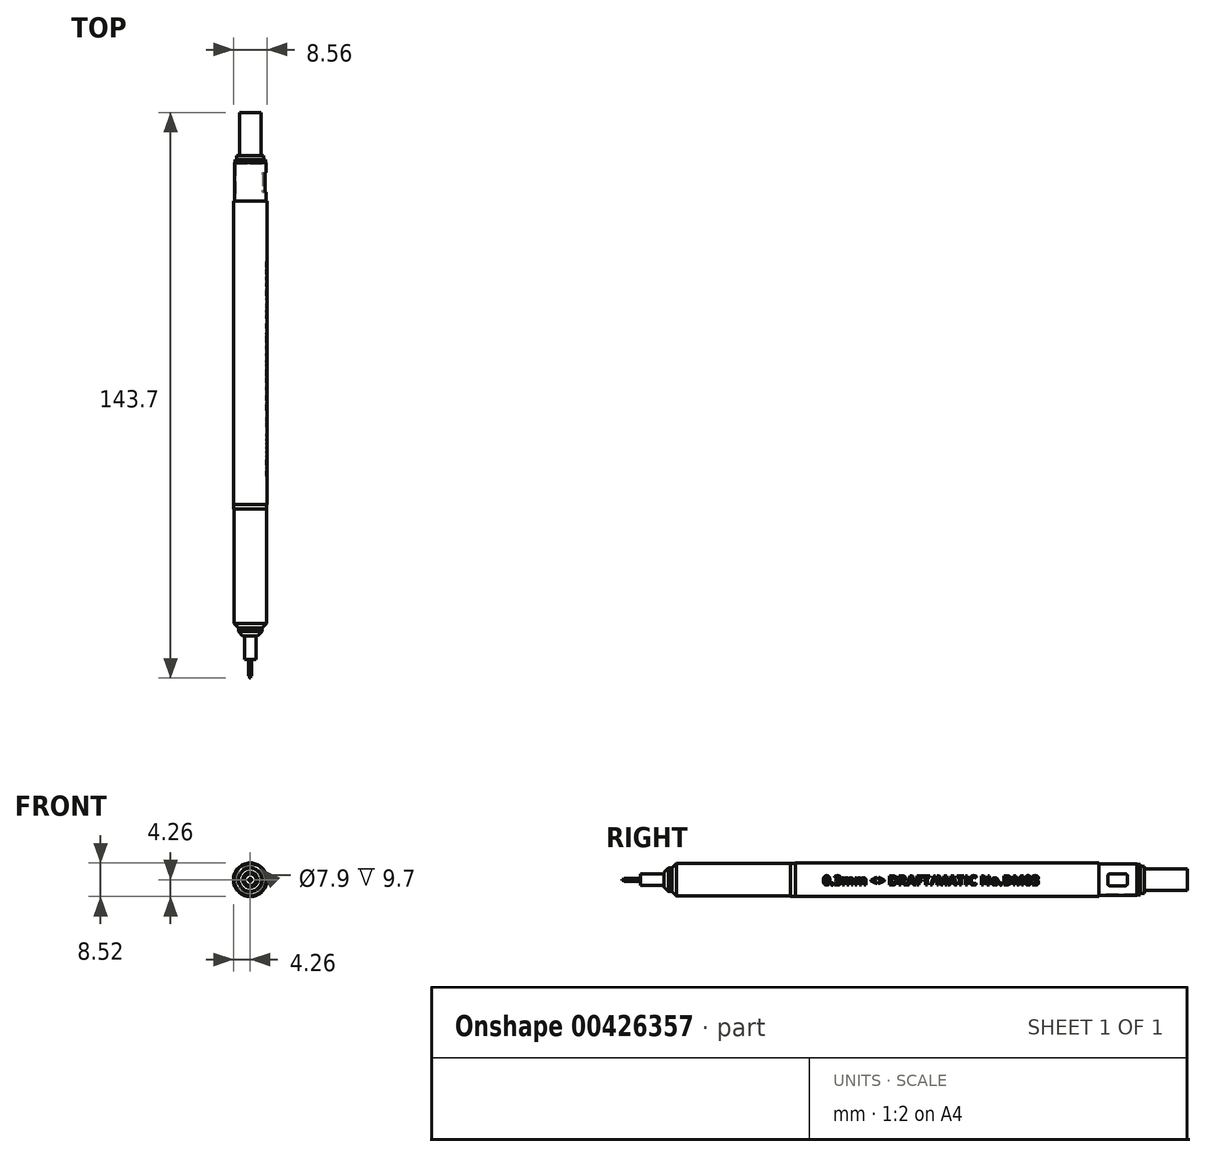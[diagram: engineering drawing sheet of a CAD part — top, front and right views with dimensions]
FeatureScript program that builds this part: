
annotation { "Feature Type Name" : "Feature", "Feature Type Description" : "" }
export const myFeature = defineFeature(function(context is Context, id is Id, definition is map)
    precondition{}
    {
        {
            var Q0;
            Q0=qCreatedBy(makeId("Front.planeOp"),FACE);
            var sketch = newSketch(context, id + "F0", { "sketchPlane" : qUnion([Q0])});
            skCircle(sketch, "E0", {"center": v(0, 0) * mm, "radius": 4.26 * mm});
            skSolve(sketch);
        }
        {
            var Q0;
            Q0 = qSketchRegion(id + "F0", true);
            extrude(context, id + "F1", {"entities" : qUnion([Q0]), "depth" : 77.1 * mm});
        }
        {
            var Q0;
            Q0=makeQuery(id+"F1.opExtrude","CAP_FACE",FACE,{"disambiguationData":[OSD([sQuery(id+"F0.wireOp",EDGE,"E0")])],"isStart":false});
            var sketch = newSketch(context, id + "F2", { "sketchPlane" : qUnion([Q0])});
            skCircle(sketch, "E1", {"center": v(0, 0) * mm, "radius": 4.2 * mm});
            skSolve(sketch);
        }
        {
            var Q0;
            Q0 = qSketchRegion(id + "F2", true);
            extrude(context, id + "F3", {"entities" : qUnion([Q0]), "depth" : 1.2 * mm});
        }
        {
            var Q0;
            Q0=makeQuery(id+"F3.opExtrude","CAP_FACE",FACE,{"disambiguationData":[OSD([sQuery(id+"F2.wireOp",EDGE,"E1")])],"isStart":false});
            var sketch = newSketch(context, id + "F4", { "sketchPlane" : qUnion([Q0])});
            skCircle(sketch, "E2", {"center": v(0, 0) * mm, "radius": 4.15 * mm});
            skSolve(sketch);
        }
        {
            var Q0;
            Q0 = qSketchRegion(id + "F4", true);
            extrude(context, id + "F5", {"entities" : qUnion([Q0]), "depth" : 29 * mm});
        }
        {
            var Q0;
            Q0=makeQuery(id+"F5.opExtrude","CAP_FACE",FACE,{"disambiguationData":[OSD([sQuery(id+"F4.wireOp",EDGE,"E2")])],"isStart":false});
            var sketch = newSketch(context, id + "F6", { "sketchPlane" : qUnion([Q0])});
            skCircle(sketch, "E3", {"center": v(0, 0) * mm, "radius": 4.15 * mm});
            skSolve(sketch);
        }
        {
            var Q0;
            Q0 = qSketchRegion(id + "F6", true);
            extrude(context, id + "F7", {"entities" : qUnion([Q0]), "depth" : 1.15 * mm, "hasDraft" : true, "draftAngle" : 45 * degree, "draftPullDirection" : true});
        }
        {
            var Q0;
            Q0=makeQuery(id+"F7.opExtrude","CAP_FACE",FACE,{"disambiguationData":[OSD([sQuery(id+"F6.wireOp",EDGE,"E3")])],"isStart":false});
            var sketch = newSketch(context, id + "F8", { "sketchPlane" : qUnion([Q0])});
            skCircle(sketch, "E4", {"center": v(0, 0) * mm, "radius": 3 * mm});
            skSolve(sketch);
        }
        {
            var Q0;
            Q0 = qSketchRegion(id + "F8", true);
            extrude(context, id + "F9", {"entities" : qUnion([Q0]), "operationType" : NewBodyOperationType.ADD, "depth" : .9 * mm});
        }
        {
            var Q0;
            Q0=makeQuery(id+"F9.opExtrude","CAP_FACE",FACE,{"disambiguationData":[OSD([sQuery(id+"F8.wireOp",EDGE,"E4")])],"isStart":false});
            var sketch = newSketch(context, id + "F10", { "sketchPlane" : qUnion([Q0])});
            skCircle(sketch, "E5", {"center": v(0, 0) * mm, "radius": 3 * mm});
            skSolve(sketch);
        }
        {
            var Q0;
            Q0 = qSketchRegion(id + "F10", true);
            extrude(context, id + "F11", {"entities" : qUnion([Q0]), "operationType" : NewBodyOperationType.ADD, "depth" : 1.1 * mm, "hasDraft" : true, "draftAngle" : 45 * degree, "draftPullDirection" : true});
        }
        {
            var Q0;
            Q0=makeQuery(id+"F11.opExtrude","CAP_FACE",FACE,{"disambiguationData":[OSD([sQuery(id+"F10.wireOp",EDGE,"E5")])],"isStart":false});
            var sketch = newSketch(context, id + "F12", { "sketchPlane" : qUnion([Q0])});
            skCircle(sketch, "E6", {"center": v(0, 0) * mm, "radius": 1.47 * mm});
            skSolve(sketch);
        }
        {
            var Q0;
            Q0 = qSketchRegion(id + "F12", true);
            extrude(context, id + "F13", {"entities" : qUnion([Q0]), "operationType" : NewBodyOperationType.ADD, "depth" : 6 * mm});
        }
        {
            var Q0;
            Q0=makeQuery(id+"F13.opExtrude","CAP_FACE",FACE,{"disambiguationData":[OSD([sQuery(id+"F12.wireOp",EDGE,"E6")])],"isStart":false});
            var sketch = newSketch(context, id + "F14", { "sketchPlane" : qUnion([Q0])});
            skCircle(sketch, "E7", {"center": v(0, 0) * mm, "radius": 0.38 * mm});
            skSolve(sketch);
        }
        {
            var Q0;
            Q0 = qSketchRegion(id + "F14", true);
            extrude(context, id + "F15", {"entities" : qUnion([Q0]), "operationType" : NewBodyOperationType.ADD, "depth" : 4.25 * mm});
        }
        {
            var Q0;
            Q0=makeQuery(id+"F1.opExtrude","CAP_FACE",FACE,{"disambiguationData":[OSD([sQuery(id+"F0.wireOp",EDGE,"E0")])],"isStart":true});
            var sketch = newSketch(context, id + "F16", { "sketchPlane" : qUnion([Q0])});
            skCircle(sketch, "E8", {"center": v(0, 0) * mm, "radius": 3.75 * mm});
            skSolve(sketch);
        }
        {
            var Q0;
            Q0 = qSketchRegion(id + "F16", true);
            extrude(context, id + "F17", {"entities" : qUnion([Q0]), "depth" : 9.5 * mm});
        }
        {
            var Q0;
            Q0=makeQuery(id+"F17.opExtrude","CAP_FACE",FACE,{"disambiguationData":[OSD([sQuery(id+"F16.wireOp",EDGE,"E8")])],"isStart":false});
            var sketch = newSketch(context, id + "F18", { "sketchPlane" : qUnion([Q0])});
            skCircle(sketch, "E9", {"center": v(0, 0) * mm, "radius": 3.9 * mm});
            skSolve(sketch);
        }
        {
            var Q0;
            Q0 = qSketchRegion(id + "F18", true);
            extrude(context, id + "F19", {"entities" : qUnion([Q0]), "depth" : 1 * mm});
        }
        {
            var Q0;
            Q0=makeQuery(id+"F19.opExtrude","CAP_FACE",FACE,{"disambiguationData":[OSD([sQuery(id+"F18.wireOp",EDGE,"E9")])],"isStart":false});
            var sketch = newSketch(context, id + "F20", { "sketchPlane" : qUnion([Q0])});
            skCircle(sketch, "E10", {"center": v(0, 0) * mm, "radius": 3.44 * mm});
            skSolve(sketch);
        }
        {
            var Q0;
            Q0 = qSketchRegion(id + "F20", true);
            extrude(context, id + "F21", {"entities" : qUnion([Q0]), "operationType" : NewBodyOperationType.ADD, "depth" : 1 * mm});
        }
        {
            var Q0;
            Q0=makeQuery(id+"F21.opExtrude","CAP_FACE",FACE,{"disambiguationData":[OSD([sQuery(id+"F20.wireOp",EDGE,"E10")])],"isStart":false});
            var sketch = newSketch(context, id + "F22", { "sketchPlane" : qUnion([Q0])});
            skCircle(sketch, "E11", {"center": v(0, 0) * mm, "radius": 2.73 * mm});
            skSolve(sketch);
        }
        {
            var Q0;
            Q0 = qSketchRegion(id + "F22", true);
            extrude(context, id + "F23", {"entities" : qUnion([Q0]), "operationType" : NewBodyOperationType.ADD, "depth" : 11 * mm});
        }
        {
            var Q0;
            Q0=makeQuery(id+"F1.opExtrude","CAP_FACE",FACE,{"disambiguationData":[OSD([sQuery(id+"F0.wireOp",EDGE,"E0")])],"isStart":true});
            var sketch = newSketch(context, id + "F24", { "sketchPlane" : qUnion([Q0])});
            skCircle(sketch, "E12", {"center": v(0, 0) * mm, "radius": 3.95 * mm});
            skCircle(sketch, "E13", {"center": v(0, 0) * mm, "radius": 4 * mm});
            skSolve(sketch);
        }
        {
            var Q0;
            Q0 = qSketchRegion(id + "F24", true);
            extrude(context, id + "F25", {"entities" : qUnion([Q0]), "depth" : 9.7 * mm});
        }
        {
            var Q0;
            Q0=qCreatedBy(makeId("Right.planeOp"),FACE);
            cPlane(context, id + "F26", {"entities" : qUnion([Q0]), "cplaneType" : CPlaneType.OFFSET, "offset" : 4.2 * mm, "width" : 150 * mm, "height" : 150 * mm});
        }
        {
            var Q0;
            Q0=qCreatedBy(id+"F26.planeOp",FACE);
            var sketch = newSketch(context, id + "F27", { "sketchPlane" : qUnion([Q0])});
            skLineSegment(sketch, "E14.bottom", {"start": v(6.75, 1.5) * mm, "end": v(2.75, 1.5) * mm});
            skLineSegment(sketch, "E14.top", {"start": v(6.75, -1.5) * mm, "end": v(2.75, -1.5) * mm});
            skLineSegment(sketch, "E14.left", {"start": v(7.25, 1) * mm, "end": v(7.25, -1) * mm});
            skLineSegment(sketch, "E14.right", {"start": v(2.25, 1) * mm, "end": v(2.25, -1) * mm});
            skPoint(sketch, "E14.middle", {"position": v(4.75, 0) * mm});
            skPoint(sketch, "E15.visualSharp", {"position": v(2.25, 1.5) * mm});
            skArc(sketch, "E15.filletArc", {"start": v(2.75, 1.5) * mm, "mid": v(2.4, 1.35) * mm, "end": v(2.25, 1) * mm});
            skPoint(sketch, "E16.visualSharp", {"position": v(2.25, -1.5) * mm});
            skArc(sketch, "E16.filletArc", {"start": v(2.25, -1) * mm, "mid": v(2.4, -1.35) * mm, "end": v(2.75, -1.5) * mm});
            skPoint(sketch, "E17.visualSharp", {"position": v(7.25, -1.5) * mm});
            skArc(sketch, "E17.filletArc", {"start": v(6.75, -1.5) * mm, "mid": v(7.1, -1.35) * mm, "end": v(7.25, -1) * mm});
            skPoint(sketch, "E18.visualSharp", {"position": v(7.25, 1.5) * mm});
            skArc(sketch, "E18.filletArc", {"start": v(7.25, 1) * mm, "mid": v(7.1, 1.35) * mm, "end": v(6.75, 1.5) * mm});
            skSolve(sketch);
        }
        {
            var Q0;
            Q0 = qSketchRegion(id + "F27", true);
            extrude(context, id + "F28", {"entities" : qUnion([Q0]), "operationType" : NewBodyOperationType.REMOVE, "oppositeDirection" : true, "depth" : 1 * mm});
        }
        {
            var Q0;
            Q0=qCreatedBy(makeId("Right.planeOp"),FACE);
            cPlane(context, id + "F29", {"entities" : qUnion([Q0]), "cplaneType" : CPlaneType.OFFSET, "offset" : 5 * mm, "width" : 150 * mm, "height" : 150 * mm});
        }
        {
            var Q0;
            Q0=qCreatedBy(id+"F29.planeOp",FACE);
            var sketch = newSketch(context, id + "F30", { "sketchPlane" : qUnion([Q0])});
            skText(sketch, "E19", { "text": "0.3mm <> DRAFT/MATIC No.DM03", "fontName": "OpenSans-Bold.ttf"});
            const initialGuessF30  = {"E19": [-0.0701, -0.00133, 1, 0, 0.00237]};
            skSetInitialGuess(sketch, initialGuessF30);
            skSolve(sketch);
        }
        {
            var Q0;
            Q0 = qSketchRegion(id + "F30", true);
            extrude(context, id + "F31", {"entities" : qUnion([Q0]), "oppositeDirection" : true, "depth" : 1 * mm});
        }
        {
            var Q0;
            Q0=makeQuery(id+"F23.opExtrude","CAP_FACE",FACE,{"disambiguationData":[OSD([sQuery(id+"F22.wireOp",EDGE,"E11")])],"isStart":false});
            var sketch = newSketch(context, id + "F32", { "sketchPlane" : qUnion([Q0])});
            skCircle(sketch, "E20", {"center": v(0, 0) * mm, "radius": 4.3 * mm});
            skCircle(sketch, "E21", {"center": v(0, 0) * mm, "radius": 6 * mm});
            skSolve(sketch);
        }
        {
            var Q0;
            Q0 = qSketchRegion(id + "F32", true);
            extrude(context, id + "F33", {"entities" : qUnion([Q0]), "operationType" : NewBodyOperationType.REMOVE, "endBound" : BoundingType.THROUGH_ALL, "oppositeDirection" : true, "depth" : 25 * mm});
        }
        {
            var Q0;
            Q0=makeQuery(id+"F15.opExtrude","CAP_FACE",FACE,{"disambiguationData":[OSD([sQuery(id+"F14.wireOp",EDGE,"E7")])],"isStart":false});
            var sketch = newSketch(context, id + "F34", { "sketchPlane" : qUnion([Q0])});
            skCircle(sketch, "E22", {"center": v(0, 0) * mm, "radius": 0.15 * mm});
            skSolve(sketch);
        }
        {
            var Q0;
            Q0 = qSketchRegion(id + "F34", true);
            extrude(context, id + "F35", {"entities" : qUnion([Q0]), "depth" : .5 * mm});
        }
    });
